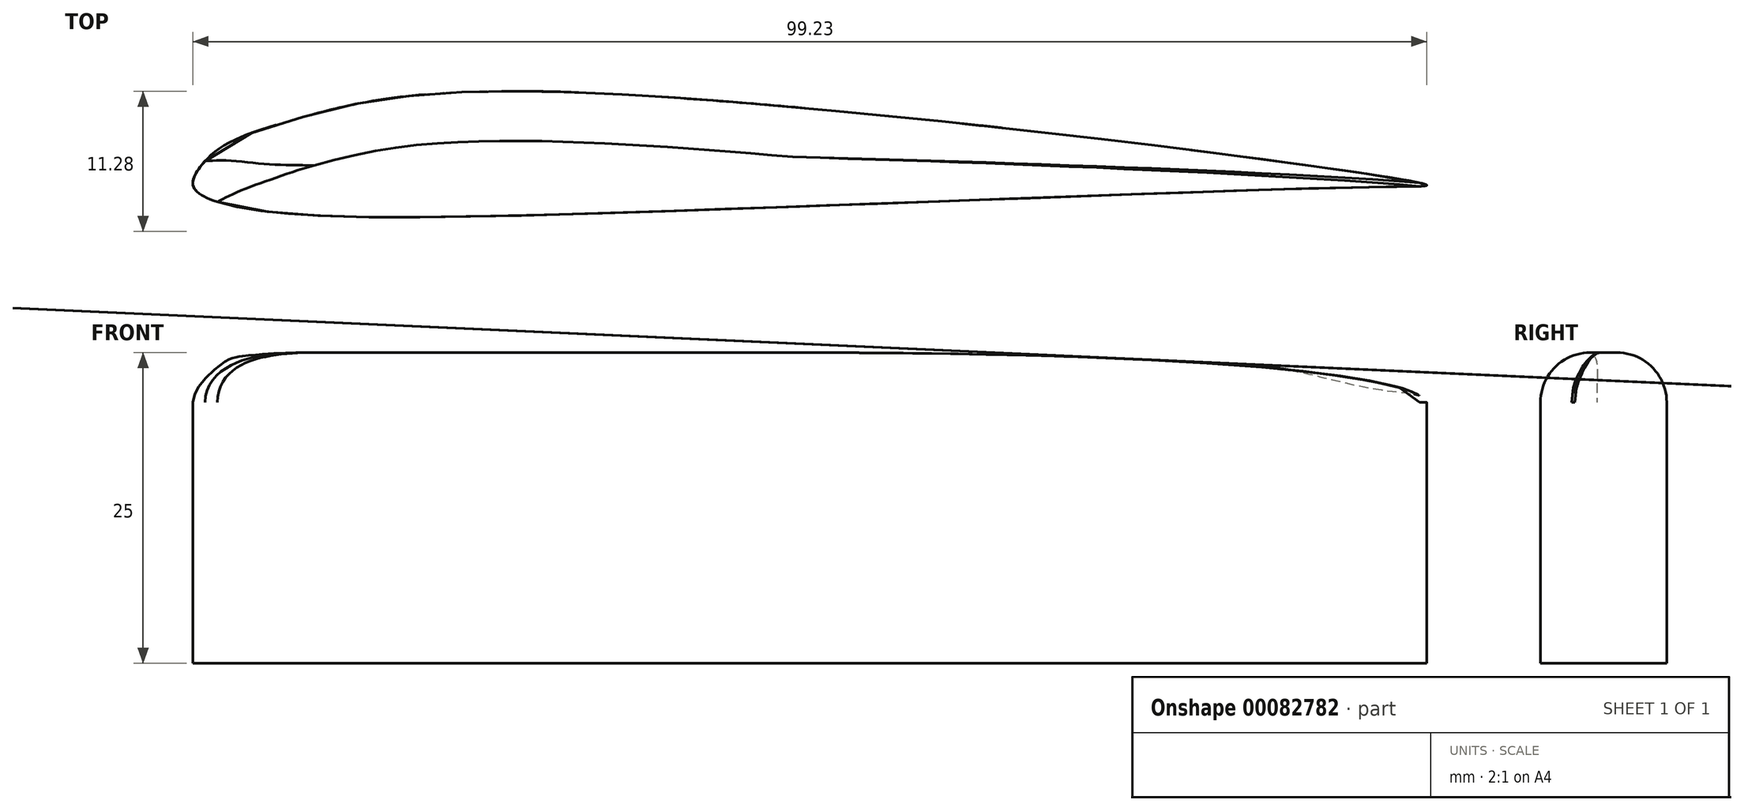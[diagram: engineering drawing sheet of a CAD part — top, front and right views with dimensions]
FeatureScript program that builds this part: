
annotation { "Feature Type Name" : "Feature", "Feature Type Description" : "" }
export const myFeature = defineFeature(function(context is Context, id is Id, definition is map)
    precondition{}
    {
        {
            var Q0;
            Q0=qCreatedBy(makeId("Top.planeOp"),FACE);
            var sketch = newSketch(context, id + "F0", { "sketchPlane" : qUnion([Q0])});
            skFitSpline(sketch, "E0", {"points": [v(58.23, 0) * mm, v(61.37, 0.2) * mm, v(-8.32, 7.64) * mm, v(-29.07, 5.55) * mm, v(-35.2, 3.33) * mm, v(-37.29, 1.37) * mm, v(-37.68, 0) * mm, v(-34.16, -1.63) * mm, v(-5.7, -2.15) * mm, v(58.23, 0) * mm]});
            skSolve(sketch);
        }
        {
            var Q0;
            Q0 = qSketchRegion(id + "F0", true);
            extrude(context, id + "F1", {"entities" : qUnion([Q0]), "depth" : 25 * mm});
        }
        {
            var Q0;
            Q0=makeQuery(id+"F1.opExtrude","CAP_EDGE",EDGE,{"disambiguationData":[OSD([sQuery(id+"F0.wireOp",EDGE,"E0")])],"isStart":false});
            fillet(context, id + "F2", {"entities" : qUnion([Q0]), "radius" : 4 * mm, "allowEdgeOverflow" : false});
        }
    });
